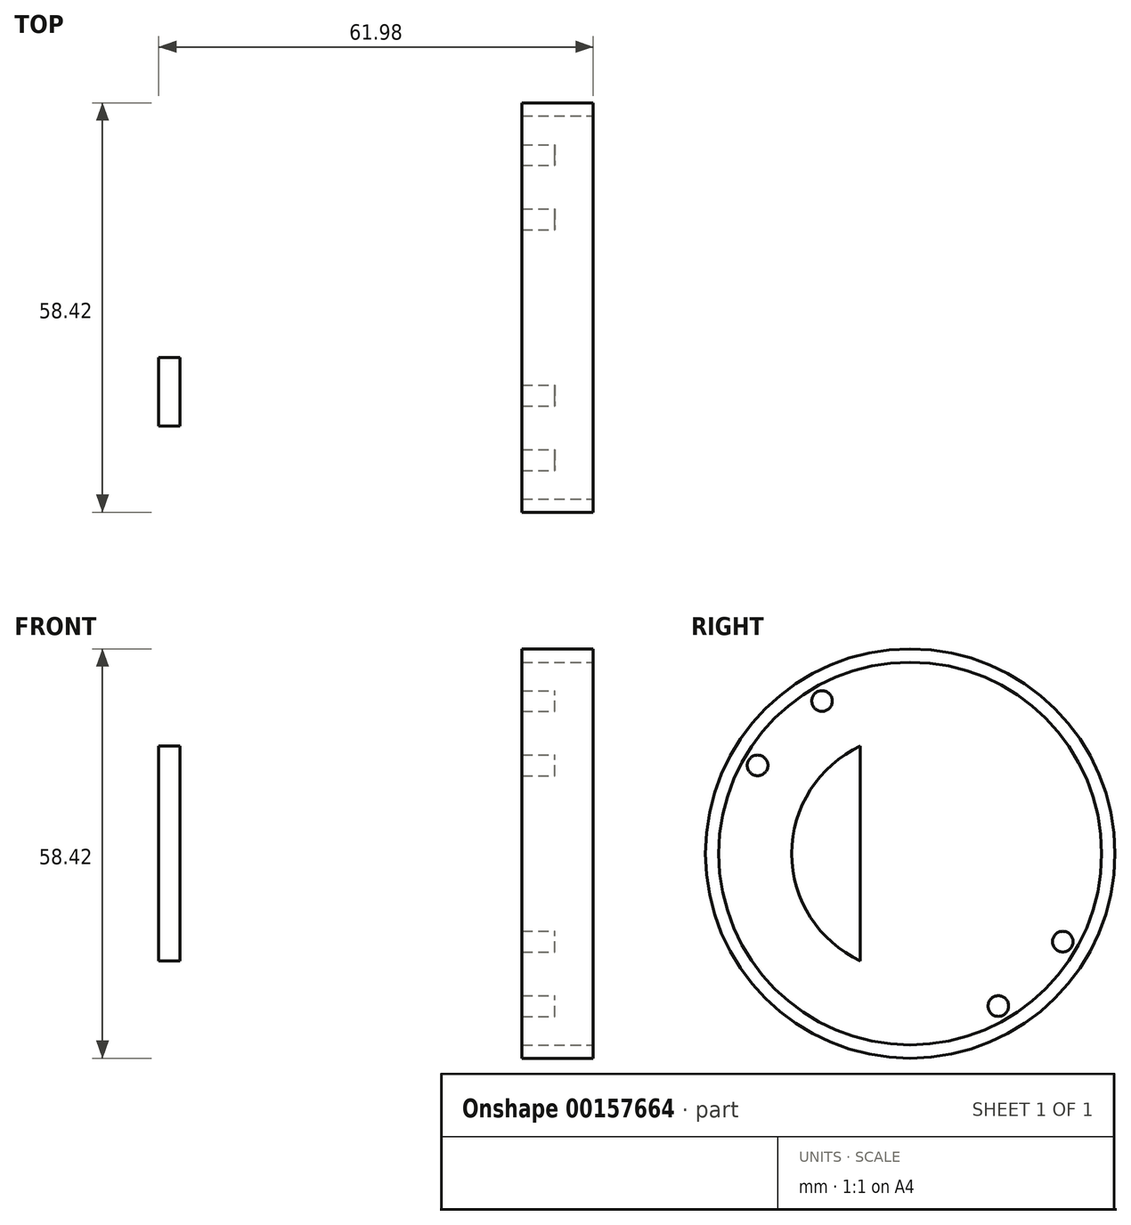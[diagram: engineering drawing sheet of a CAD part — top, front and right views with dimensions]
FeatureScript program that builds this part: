
annotation { "Feature Type Name" : "Feature", "Feature Type Description" : "" }
export const myFeature = defineFeature(function(context is Context, id is Id, definition is map)
    precondition{}
    {
        {
            var Q0;
            Q0=qCreatedBy(makeId("Right.planeOp"),FACE);
            var sketch = newSketch(context, id + "F0", { "sketchPlane" : qUnion([Q0])});
            skCircle(sketch, "E0", {"center": v(0, 0) * mm, "radius": 29.21 * mm});
            skCircle(sketch, "E1", {"center": v(0, 0) * mm, "radius": 16.9 * mm});
            skSolve(sketch);
        }
        {
            var Q0;
            Q0=makeQuery(id+"F0.imprint","IMPRINT",FACE,{"disambiguationData":[TD([[makeQuery(id+"F0.imprint","IMPRINT",EDGE,{"derivedFrom":sQuery(id+"F0.wireOp",EDGE,"E0")}),1.0]])]});
            extrude(context, id + "F1", {"entities" : qUnion([Q0]), "oppositeDirection" : true, "depth" : 10.16 * mm});
        }
        {
            var Q0;
            Q0=makeQuery(id+"F1.opExtrude","CAP_FACE",FACE,{"disambiguationData":[OSD([sQuery(id+"F0.wireOp",EDGE,"E0"),sQuery(id+"F0.wireOp",EDGE,"E1")])],"isStart":false});
            var sketch = newSketch(context, id + "F2", { "sketchPlane" : qUnion([Q0])});
            skCircle(sketch, "E2", {"center": v(0, 0) * mm, "radius": 20.07 * mm});
            skSolve(sketch);
        }
        {
            var Q0;
            Q0=makeQuery(id+"F2.imprint","IMPRINT",FACE,{"disambiguationData":[TD([[makeQuery(id+"F2.imprint","IMPRINT",EDGE,{"derivedFrom":sQuery(id+"F2.wireOp",EDGE,"E2")}),1.0]])]});
            var Q1;
            Q1=makeQuery(id+"F2.imprint","IMPRINT",FACE,{"disambiguationData":[TD([[makeQuery(id+"F2.imprint","IMPRINT",EDGE,{"derivedFrom":makeQuery(id+"F1.opExtrude","CAP_EDGE",EDGE,{"disambiguationData":[OSD([sQuery(id+"F0.wireOp",EDGE,"E1")])],"isStart":false})}),-1.0]])]});
            extrude(context, id + "F3", {"entities" : qUnion([Q0, Q1]), "operationType" : NewBodyOperationType.ADD, "depth" : 51.82 * mm});
        }
        {
            var Q0;
            Q0=makeQuery(id+"F3.opExtrude","CAP_FACE",FACE,{"disambiguationData":[OSD([sQuery(id+"F2.wireOp",EDGE,"E2")])],"isStart":true});
            extrude(context, id + "F4", {"entities" : qUnion([Q0]), "operationType" : NewBodyOperationType.REMOVE, "oppositeDirection" : true, "depth" : 48.77 * mm});
        }
        {
            var Q0;
            Q0=makeQuery(id+"F1.opExtrude","CAP_FACE",FACE,{"disambiguationData":[OSD([sQuery(id+"F0.wireOp",EDGE,"E0"),sQuery(id+"F0.wireOp",EDGE,"E1")])],"isStart":true});
            var sketch = newSketch(context, id + "F5", { "sketchPlane" : qUnion([Q0])});
            skCircle(sketch, "E3", {"center": v(0, 0) * mm, "radius": 27.31 * mm});
            skSolve(sketch);
        }
        {
            var Q0;
            Q0=makeQuery(id+"F5.imprint","IMPRINT",FACE,{"disambiguationData":[TD([[makeQuery(id+"F5.imprint","IMPRINT",EDGE,{"derivedFrom":sQuery(id+"F5.wireOp",EDGE,"E3")}),1.0]])]});
            extrude(context, id + "F6", {"entities" : qUnion([Q0]), "operationType" : NewBodyOperationType.REMOVE, "oppositeDirection" : true, "depth" : 5.46 * mm});
        }
        {
            var Q0;
            Q0=makeQuery(id+"F6.boolean.opBoolean","COPY",FACE,{"derivedFrom":makeQuery(id+"F6.opExtrude","CAP_FACE",FACE,{"disambiguationData":[OSD([sQuery(id+"F0.wireOp",EDGE,"E1"),sQuery(id+"F5.wireOp",EDGE,"E3")])],"isStart":false})});
            var sketch = newSketch(context, id + "F7", { "sketchPlane" : qUnion([Q0])});
            skCircle(sketch, "E4", {"center": v(12.57, 21.77) * mm, "radius": 1.47 * mm});
            skCircle(sketch, "E5", {"center": v(21.77, 12.57) * mm, "radius": 1.47 * mm});
            skCircle(sketch, "E6.MirrorC", {"center": v(-12.57, 21.77) * mm, "radius": 1.47 * mm});
            skCircle(sketch, "E7.MirrorC", {"center": v(-21.77, 12.57) * mm, "radius": 1.47 * mm});
            skCircle(sketch, "E8.MirrorC", {"center": v(-21.77, -12.57) * mm, "radius": 1.47 * mm});
            skCircle(sketch, "E9.MirrorC", {"center": v(-12.57, -21.77) * mm, "radius": 1.47 * mm});
            skCircle(sketch, "E10.MirrorC", {"center": v(12.57, -21.77) * mm, "radius": 1.47 * mm});
            skCircle(sketch, "E11.MirrorC", {"center": v(21.77, -12.57) * mm, "radius": 1.47 * mm});
            skSolve(sketch);
        }
        {
            var Q0;
            Q0=makeQuery(id+"F7.imprint","IMPRINT",FACE,{"disambiguationData":[TD([[makeQuery(id+"F7.imprint","IMPRINT",EDGE,{"derivedFrom":sQuery(id+"F7.wireOp",EDGE,"E6.MirrorC")}),-1.0]])]});
            var Q1;
            Q1=makeQuery(id+"F7.imprint","IMPRINT",FACE,{"disambiguationData":[TD([[makeQuery(id+"F7.imprint","IMPRINT",EDGE,{"derivedFrom":sQuery(id+"F7.wireOp",EDGE,"E4")}),1.0]])]});
            var Q2;
            Q2=makeQuery(id+"F7.imprint","IMPRINT",FACE,{"disambiguationData":[TD([[makeQuery(id+"F7.imprint","IMPRINT",EDGE,{"derivedFrom":sQuery(id+"F7.wireOp",EDGE,"E5")}),1.0]])]});
            var Q3;
            Q3=makeQuery(id+"F7.imprint","IMPRINT",FACE,{"disambiguationData":[TD([[makeQuery(id+"F7.imprint","IMPRINT",EDGE,{"derivedFrom":sQuery(id+"F7.wireOp",EDGE,"E11.MirrorC")}),-1.0]])]});
            var Q4;
            Q4=makeQuery(id+"F7.imprint","IMPRINT",FACE,{"disambiguationData":[TD([[makeQuery(id+"F7.imprint","IMPRINT",EDGE,{"derivedFrom":sQuery(id+"F7.wireOp",EDGE,"E10.MirrorC")}),-1.0]])]});
            var Q5;
            Q5=makeQuery(id+"F7.imprint","IMPRINT",FACE,{"disambiguationData":[TD([[makeQuery(id+"F7.imprint","IMPRINT",EDGE,{"derivedFrom":sQuery(id+"F7.wireOp",EDGE,"E9.MirrorC")}),1.0]])]});
            var Q6;
            Q6=makeQuery(id+"F7.imprint","IMPRINT",FACE,{"disambiguationData":[TD([[makeQuery(id+"F7.imprint","IMPRINT",EDGE,{"derivedFrom":sQuery(id+"F7.wireOp",EDGE,"E8.MirrorC")}),1.0]])]});
            var Q7;
            Q7=makeQuery(id+"F7.imprint","IMPRINT",FACE,{"disambiguationData":[TD([[makeQuery(id+"F7.imprint","IMPRINT",EDGE,{"derivedFrom":sQuery(id+"F7.wireOp",EDGE,"E7.MirrorC")}),-1.0]])]});
            extrude(context, id + "F8", {"entities" : qUnion([Q0, Q1, Q2, Q3, Q4, Q5, Q6, Q7]), "operationType" : NewBodyOperationType.REMOVE, "endBound" : BoundingType.THROUGH_ALL, "oppositeDirection" : true, "depth" : 25.4 * mm});
        }
        {
            var Q0;
            Q0=qCreatedBy(makeId("Top.planeOp"),FACE);
            cPlane(context, id + "F9", {"entities" : qUnion([Q0]), "cplaneType" : CPlaneType.OFFSET, "offset" : 20.07 * mm, "width" : 152.4 * mm, "height" : 152.4 * mm});
        }
        {
            var Q0;
            Q0=qCreatedBy(id+"F9.planeOp",FACE);
            var sketch = newSketch(context, id + "F10", { "sketchPlane" : qUnion([Q0])});
            skLineSegment(sketch, "E12", {"start": v(-19.81, 20.07) * mm, "end": v(-19.81, 29.2) * mm, "construction": true});
            skArc(sketch, "E13", {"start": v(-51.23, -7.11) * mm, "mid": v(-37.37, 53.2) * mm, "end": v(-76.18, 5) * mm});
            skLineSegment(sketch, "E14", {"start": v(-76.18, -7.11) * mm, "end": v(-76.18, 5) * mm});
            skLineSegment(sketch, "E15", {"start": v(-19.81, 25.47) * mm, "end": v(-19.74, 20.6) * mm});
            skLineSegment(sketch, "E16", {"start": v(-76.18, -7.11) * mm, "end": v(-51.23, -7.11) * mm});
            skPoint(sketch, "E17.orphan", {"position": v(-19.81, 50.94) * mm});
            skPoint(sketch, "E18.end.orphan", {"position": v(-19.81, 0) * mm});
            skSolve(sketch);
        }
        {
            var Q0;
            {var subQ0=sQuery(id+"F10.wireOp",EDGE,"E16");Q0=makeQuery(id+"F10.imprint","IMPRINT",FACE,{"disambiguationData":[TD([[makeQuery(id+"F10.imprint","IMPRINT",EDGE,{"derivedFrom":subQ0}),1.0]])]});}
            extrude(context, id + "F11", {"entities" : qUnion([Q0]), "operationType" : NewBodyOperationType.REMOVE, "endBound" : BoundingType.THROUGH_ALL, "oppositeDirection" : true, "depth" : 25.4 * mm});
        }
    });
